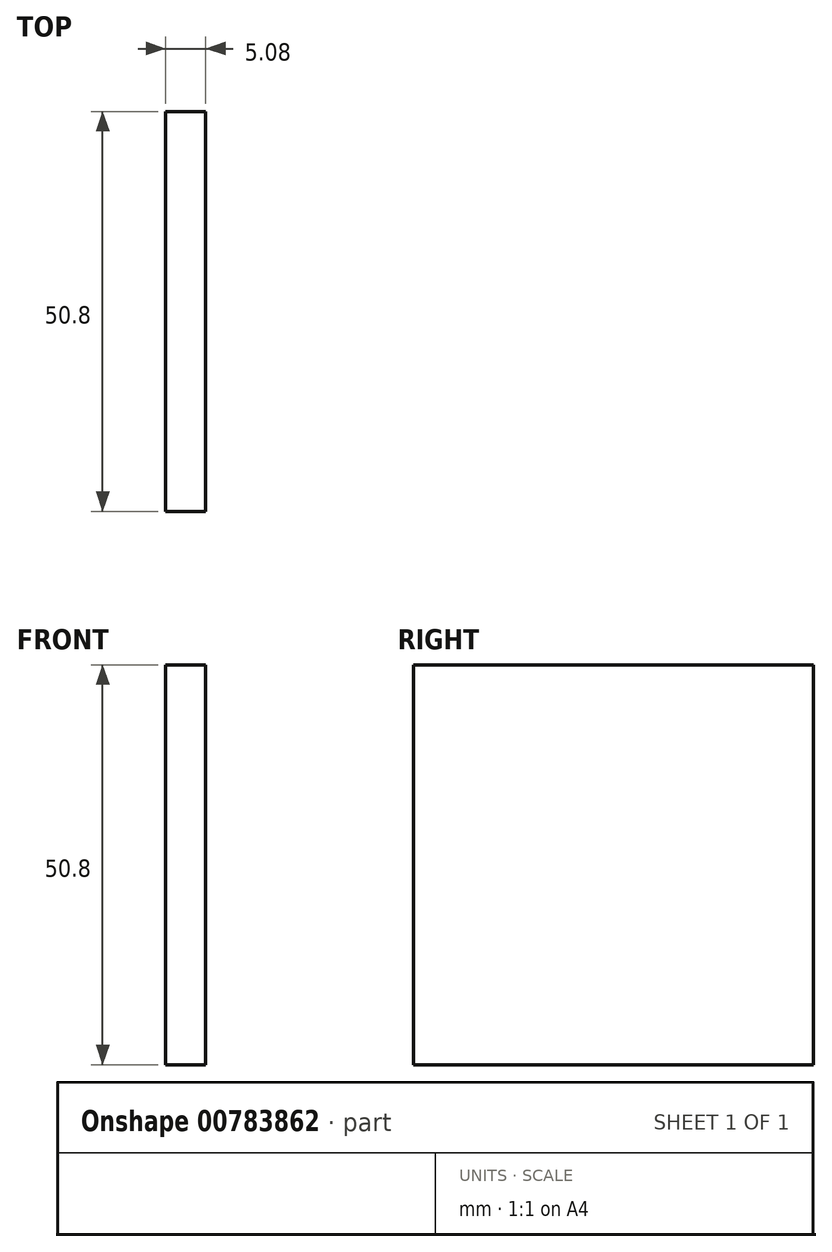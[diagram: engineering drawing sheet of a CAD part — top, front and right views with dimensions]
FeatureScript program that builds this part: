
annotation { "Feature Type Name" : "Feature", "Feature Type Description" : "" }
export const myFeature = defineFeature(function(context is Context, id is Id, definition is map)
    precondition{}
    {
        {
            var Q0;
            Q0=qCreatedBy(makeId("Right.planeOp"),FACE);
            var sketch = newSketch(context, id + "F0", { "sketchPlane" : qUnion([Q0])});
            skLineSegment(sketch, "E0.bottom", {"start": v(25.4, 25.4) * mm, "end": v(-25.4, 25.4) * mm});
            skLineSegment(sketch, "E0.top", {"start": v(25.4, -25.4) * mm, "end": v(-25.4, -25.4) * mm});
            skLineSegment(sketch, "E0.left", {"start": v(25.4, 25.4) * mm, "end": v(25.4, -25.4) * mm});
            skLineSegment(sketch, "E0.right", {"start": v(-25.4, 25.4) * mm, "end": v(-25.4, -25.4) * mm});
            skPoint(sketch, "E0.middle", {"position": v(0, 0) * mm});
            skSolve(sketch);
        }
        {
            var Q0;
            Q0=makeQuery(id+"F0.imprint","IMPRINT",FACE,{"disambiguationData":[TD([[makeQuery(id+"F0.imprint","IMPRINT",EDGE,{"derivedFrom":sQuery(id+"F0.wireOp",EDGE,"E0.bottom")}),1.0]])]});
            extrude(context, id + "F1", {"entities" : qUnion([Q0]), "depth" : 5.08 * mm, "offsetDistance" : 25.4 * mm});
        }
    });
